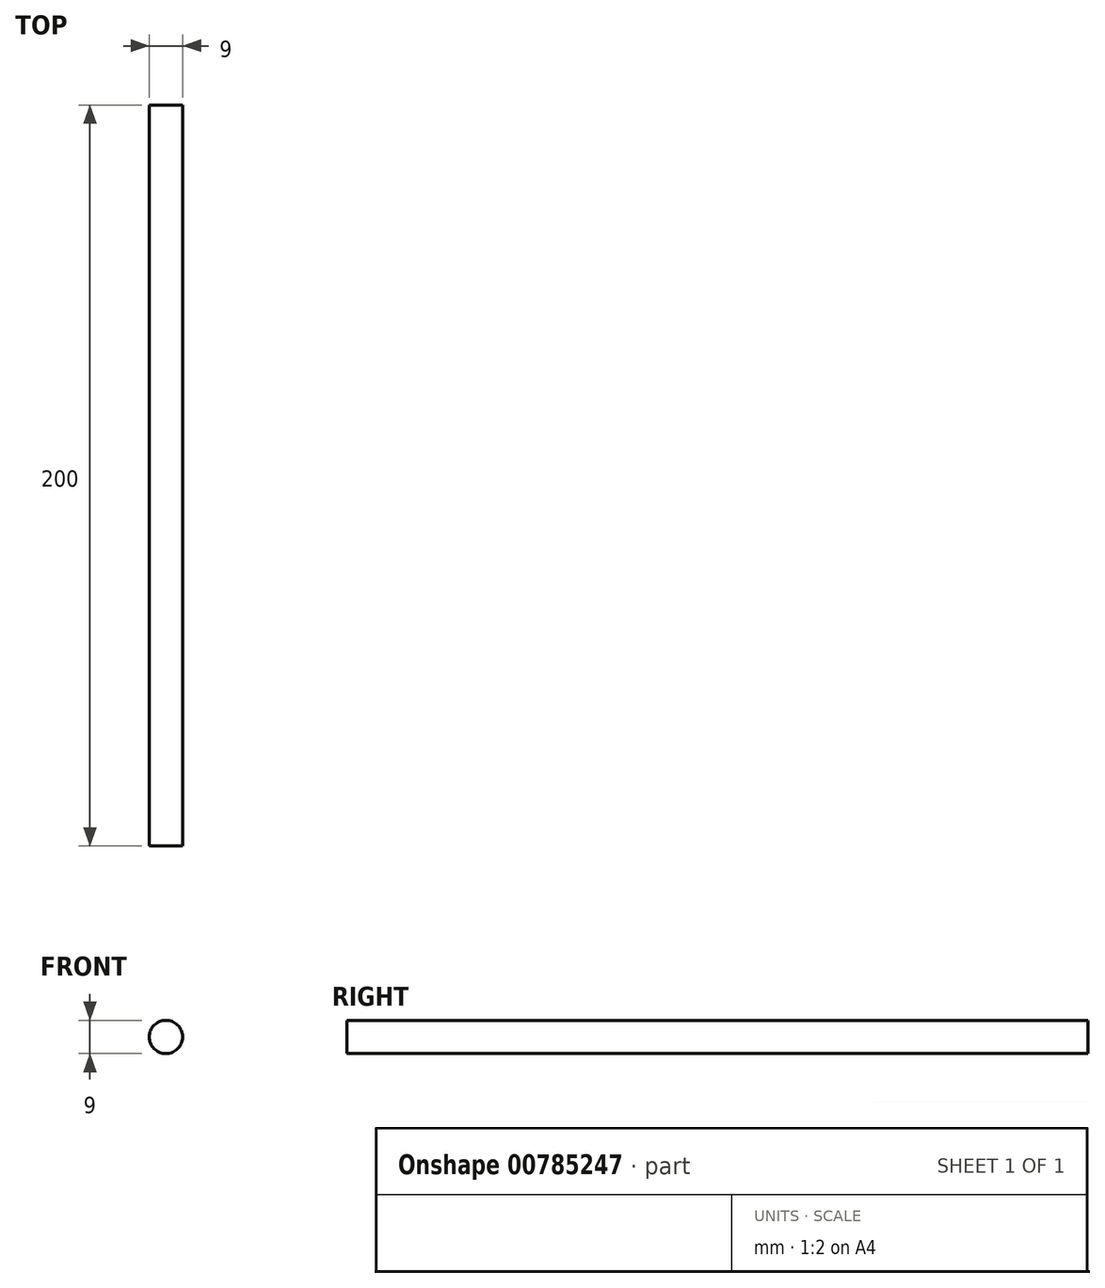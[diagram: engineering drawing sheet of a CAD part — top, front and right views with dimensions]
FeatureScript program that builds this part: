
annotation { "Feature Type Name" : "Feature", "Feature Type Description" : "" }
export const myFeature = defineFeature(function(context is Context, id is Id, definition is map)
    precondition{}
    {
        {
            var Q0;
            Q0=qCreatedBy(makeId("Front.planeOp"),FACE);
            var sketch = newSketch(context, id + "F0", { "sketchPlane" : qUnion([Q0])});
            skCircle(sketch, "E0", {"center": v(0, 0) * mm, "radius": 4.5 * mm});
            skSolve(sketch);
        }
        {
            var Q0;
            Q0=makeQuery(id+"F0.imprint","IMPRINT",FACE,{"disambiguationData":[TD([[makeQuery(id+"F0.imprint","IMPRINT",EDGE,{"derivedFrom":sQuery(id+"F0.wireOp",EDGE,"E0")}),1.0]])]});
            extrude(context, id + "F1", {"entities" : qUnion([Q0]), "depth" : 200 * mm, "offsetDistance" : 25 * mm});
        }
    });
